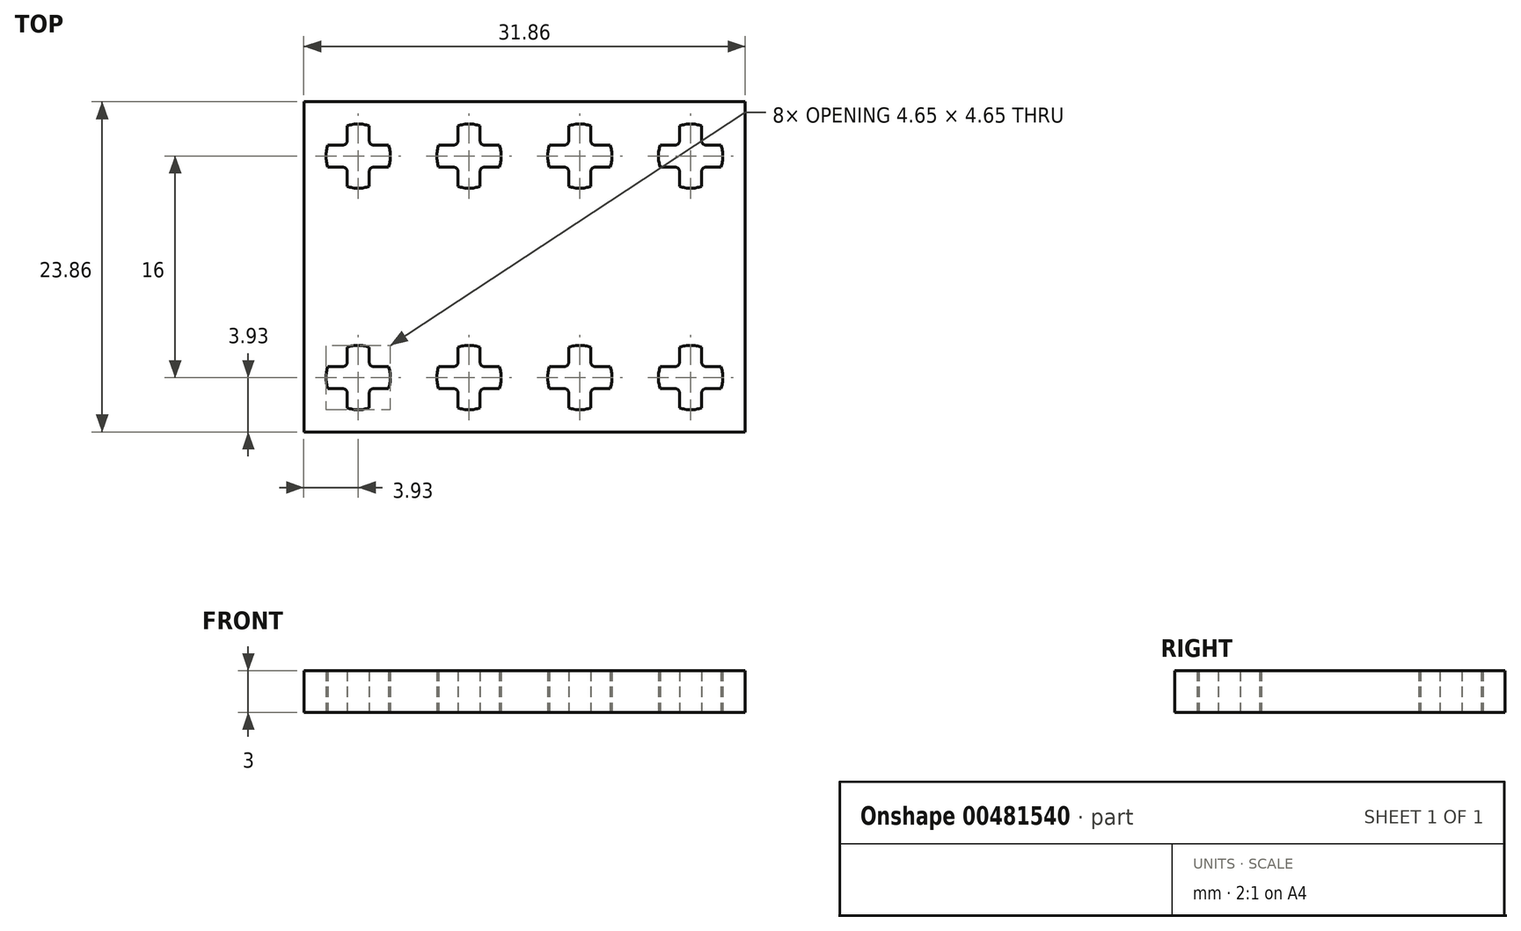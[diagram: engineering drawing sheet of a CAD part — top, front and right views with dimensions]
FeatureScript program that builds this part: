
annotation { "Feature Type Name" : "Feature", "Feature Type Description" : "" }
export const myFeature = defineFeature(function(context is Context, id is Id, definition is map)
    precondition{}
    {
        {
            var Q0;
            Q0=qCreatedBy(makeId("Top.planeOp"),FACE);
            var sketch = newSketch(context, id + "F0", { "sketchPlane" : qUnion([Q0])});
            skLineSegment(sketch, "E0.bottom", {"start": v(-16, 12) * mm, "end": v(16, 12) * mm, "construction": true});
            skLineSegment(sketch, "E0.top", {"start": v(-16, -12) * mm, "end": v(16, -12) * mm, "construction": true});
            skLineSegment(sketch, "E0.left", {"start": v(-16, 12) * mm, "end": v(-16, -12) * mm, "construction": true});
            skLineSegment(sketch, "E0.right", {"start": v(16, 12) * mm, "end": v(16, -12) * mm, "construction": true});
            skLineSegment(sketch, "E1", {"start": v(-12.8, 10.18) * mm, "end": v(-11.2, 10.18) * mm, "construction": true});
            skLineSegment(sketch, "E2", {"start": v(-11.2, 10.18) * mm, "end": v(-11.2, 9.1) * mm});
            skLineSegment(sketch, "E3", {"start": v(-10.9, 8.8) * mm, "end": v(-9.82, 8.8) * mm});
            skLineSegment(sketch, "E4", {"start": v(-9.82, 8.8) * mm, "end": v(-12, 8) * mm, "construction": true});
            skLineSegment(sketch, "E5", {"start": v(-12, 8) * mm, "end": v(-12.8, 10.18) * mm, "construction": true});
            skArc(sketch, "E6", {"start": v(-11.2, 10.18) * mm, "mid": v(-12, 10.33) * mm, "end": v(-12.8, 10.18) * mm});
            skArc(sketch, "E7", {"start": v(-11.2, 9.1) * mm, "mid": v(-11.11, 8.89) * mm, "end": v(-10.9, 8.8) * mm});
            skLineSegment(sketch, "E8", {"start": v(-11.2, 10.18) * mm, "end": v(-11.2, 8.8) * mm, "construction": true});
            skLineSegment(sketch, "E9", {"start": v(-11.2, 8.8) * mm, "end": v(-9.82, 8.8) * mm, "construction": true});
            skArc(sketch, "E10.1.0", {"start": v(-14.18, 8.8) * mm, "mid": v(-14.32, 8) * mm, "end": v(-14.18, 7.2) * mm});
            skArc(sketch, "E10.1.1", {"start": v(-13.1, 8.8) * mm, "mid": v(-12.89, 8.89) * mm, "end": v(-12.8, 9.1) * mm});
            skLineSegment(sketch, "E10.1.2", {"start": v(-14.18, 8.8) * mm, "end": v(-13.1, 8.8) * mm});
            skLineSegment(sketch, "E10.1.3", {"start": v(-12.8, 9.1) * mm, "end": v(-12.8, 10.18) * mm});
            skArc(sketch, "E10.2.0", {"start": v(-12.8, 5.82) * mm, "mid": v(-12, 5.67) * mm, "end": v(-11.2, 5.82) * mm});
            skArc(sketch, "E10.2.1", {"start": v(-12.8, 6.9) * mm, "mid": v(-12.89, 7.11) * mm, "end": v(-13.1, 7.2) * mm});
            skLineSegment(sketch, "E10.2.2", {"start": v(-12.8, 5.82) * mm, "end": v(-12.8, 6.9) * mm});
            skLineSegment(sketch, "E10.2.3", {"start": v(-13.1, 7.2) * mm, "end": v(-14.18, 7.2) * mm});
            skArc(sketch, "E10.3.0", {"start": v(-9.82, 7.2) * mm, "mid": v(-9.67, 8) * mm, "end": v(-9.82, 8.8) * mm});
            skArc(sketch, "E10.3.1", {"start": v(-10.9, 7.2) * mm, "mid": v(-11.11, 7.11) * mm, "end": v(-11.2, 6.9) * mm});
            skLineSegment(sketch, "E10.3.2", {"start": v(-9.82, 7.2) * mm, "end": v(-10.9, 7.2) * mm});
            skLineSegment(sketch, "E10.3.3", {"start": v(-11.2, 6.9) * mm, "end": v(-11.2, 5.82) * mm});
            skArc(sketch, "E11.1.0.0", {"start": v(-3.2, 10.18) * mm, "mid": v(-4, 10.32) * mm, "end": v(-4.8, 10.18) * mm});
            skArc(sketch, "E11.1.0.1", {"start": v(-2.9, 7.2) * mm, "mid": v(-3.11, 7.11) * mm, "end": v(-3.2, 6.9) * mm});
            skLineSegment(sketch, "E11.1.0.2", {"start": v(-1.82, 7.2) * mm, "end": v(-2.9, 7.2) * mm});
            skLineSegment(sketch, "E11.1.0.3", {"start": v(-5.1, 7.2) * mm, "end": v(-6.18, 7.2) * mm});
            skArc(sketch, "E11.1.0.4", {"start": v(-4.8, 6.9) * mm, "mid": v(-4.89, 7.11) * mm, "end": v(-5.1, 7.2) * mm});
            skLineSegment(sketch, "E11.1.0.5", {"start": v(-4.8, 9.1) * mm, "end": v(-4.8, 10.18) * mm});
            skLineSegment(sketch, "E11.1.0.6", {"start": v(-6.18, 8.8) * mm, "end": v(-5.1, 8.8) * mm});
            skArc(sketch, "E11.1.0.7", {"start": v(-5.1, 8.8) * mm, "mid": v(-4.89, 8.89) * mm, "end": v(-4.8, 9.1) * mm});
            skArc(sketch, "E11.1.0.8", {"start": v(-4.8, 5.82) * mm, "mid": v(-4, 5.67) * mm, "end": v(-3.2, 5.82) * mm});
            skArc(sketch, "E11.1.0.9", {"start": v(-6.18, 8.8) * mm, "mid": v(-6.32, 8) * mm, "end": v(-6.18, 7.2) * mm});
            skPoint(sketch, "E11.1.0.10", {"position": v(-4, 8) * mm});
            skLineSegment(sketch, "E11.1.0.11", {"start": v(-4.8, 5.82) * mm, "end": v(-4.8, 6.9) * mm});
            skArc(sketch, "E11.1.0.12", {"start": v(-1.82, 7.2) * mm, "mid": v(-1.67, 8) * mm, "end": v(-1.82, 8.8) * mm});
            skLineSegment(sketch, "E11.1.0.13", {"start": v(-3.2, 6.9) * mm, "end": v(-3.2, 5.82) * mm});
            skLineSegment(sketch, "E11.1.0.14", {"start": v(-3.2, 10.18) * mm, "end": v(-3.2, 9.1) * mm});
            skLineSegment(sketch, "E11.1.0.15", {"start": v(-2.9, 8.8) * mm, "end": v(-1.82, 8.8) * mm});
            skArc(sketch, "E11.1.0.16", {"start": v(-3.2, 9.1) * mm, "mid": v(-3.11, 8.89) * mm, "end": v(-2.9, 8.8) * mm});
            skArc(sketch, "E11.2.0.0", {"start": v(4.8, 10.18) * mm, "mid": v(4, 10.32) * mm, "end": v(3.2, 10.18) * mm});
            skArc(sketch, "E11.2.0.1", {"start": v(5.1, 7.2) * mm, "mid": v(4.89, 7.11) * mm, "end": v(4.8, 6.9) * mm});
            skLineSegment(sketch, "E11.2.0.2", {"start": v(6.18, 7.2) * mm, "end": v(5.1, 7.2) * mm});
            skLineSegment(sketch, "E11.2.0.3", {"start": v(2.9, 7.2) * mm, "end": v(1.82, 7.2) * mm});
            skArc(sketch, "E11.2.0.4", {"start": v(3.2, 6.9) * mm, "mid": v(3.11, 7.11) * mm, "end": v(2.9, 7.2) * mm});
            skLineSegment(sketch, "E11.2.0.5", {"start": v(3.2, 9.1) * mm, "end": v(3.2, 10.18) * mm});
            skLineSegment(sketch, "E11.2.0.6", {"start": v(1.82, 8.8) * mm, "end": v(2.9, 8.8) * mm});
            skArc(sketch, "E11.2.0.7", {"start": v(2.9, 8.8) * mm, "mid": v(3.11, 8.89) * mm, "end": v(3.2, 9.1) * mm});
            skArc(sketch, "E11.2.0.8", {"start": v(3.2, 5.82) * mm, "mid": v(4, 5.67) * mm, "end": v(4.8, 5.82) * mm});
            skArc(sketch, "E11.2.0.9", {"start": v(1.82, 8.8) * mm, "mid": v(1.68, 8) * mm, "end": v(1.82, 7.2) * mm});
            skPoint(sketch, "E11.2.0.10", {"position": v(4, 8) * mm});
            skLineSegment(sketch, "E11.2.0.11", {"start": v(3.2, 5.82) * mm, "end": v(3.2, 6.9) * mm});
            skArc(sketch, "E11.2.0.12", {"start": v(6.18, 7.2) * mm, "mid": v(6.33, 8) * mm, "end": v(6.18, 8.8) * mm});
            skLineSegment(sketch, "E11.2.0.13", {"start": v(4.8, 6.9) * mm, "end": v(4.8, 5.82) * mm});
            skLineSegment(sketch, "E11.2.0.14", {"start": v(4.8, 10.18) * mm, "end": v(4.8, 9.1) * mm});
            skLineSegment(sketch, "E11.2.0.15", {"start": v(5.1, 8.8) * mm, "end": v(6.18, 8.8) * mm});
            skArc(sketch, "E11.2.0.16", {"start": v(4.8, 9.1) * mm, "mid": v(4.89, 8.89) * mm, "end": v(5.1, 8.8) * mm});
            skLineSegment(sketch, "E11.direction1", {"start": v(-12.8, 5.82) * mm, "end": v(-4.8, 5.82) * mm, "construction": true});
            skLineSegment(sketch, "E11.direction2", {"start": v(-12.8, 5.82) * mm, "end": v(-12.8, -2.18) * mm, "construction": true});
            skLineSegment(sketch, "E12.bottom", {"start": v(-15.93, 11.93) * mm, "end": v(15.93, 11.92) * mm});
            skLineSegment(sketch, "E12.top", {"start": v(-15.93, -11.93) * mm, "end": v(15.92, -11.93) * mm});
            skLineSegment(sketch, "E12.left", {"start": v(-15.92, 11.92) * mm, "end": v(-15.92, -11.92) * mm});
            skLineSegment(sketch, "E12.right", {"start": v(15.93, 11.93) * mm, "end": v(15.93, -11.92) * mm});
            skArc(sketch, "E13.0.3.0", {"start": v(12.8, 10.18) * mm, "mid": v(12, 10.32) * mm, "end": v(11.2, 10.18) * mm});
            skArc(sketch, "E13.4.3.0", {"start": v(13.1, 7.2) * mm, "mid": v(12.89, 7.11) * mm, "end": v(12.8, 6.9) * mm});
            skLineSegment(sketch, "E13.8.3.0", {"start": v(14.18, 7.2) * mm, "end": v(13.1, 7.2) * mm});
            skLineSegment(sketch, "E13.11.3.0", {"start": v(10.9, 7.2) * mm, "end": v(9.82, 7.2) * mm});
            skArc(sketch, "E13.14.3.0", {"start": v(11.2, 6.9) * mm, "mid": v(11.11, 7.11) * mm, "end": v(10.9, 7.2) * mm});
            skLineSegment(sketch, "E13.18.3.0", {"start": v(11.2, 9.1) * mm, "end": v(11.2, 10.18) * mm});
            skLineSegment(sketch, "E13.21.3.0", {"start": v(9.82, 8.8) * mm, "end": v(10.9, 8.8) * mm});
            skArc(sketch, "E13.24.3.0", {"start": v(10.9, 8.8) * mm, "mid": v(11.11, 8.89) * mm, "end": v(11.2, 9.1) * mm});
            skArc(sketch, "E13.28.3.0", {"start": v(11.2, 5.82) * mm, "mid": v(12, 5.67) * mm, "end": v(12.8, 5.82) * mm});
            skArc(sketch, "E13.32.3.0", {"start": v(9.82, 8.8) * mm, "mid": v(9.68, 8) * mm, "end": v(9.82, 7.2) * mm});
            skPoint(sketch, "E13.36.3.0", {"position": v(12, 8) * mm});
            skLineSegment(sketch, "E13.37.3.0", {"start": v(11.2, 5.82) * mm, "end": v(11.2, 6.9) * mm});
            skArc(sketch, "E13.40.3.0", {"start": v(14.18, 7.2) * mm, "mid": v(14.33, 8) * mm, "end": v(14.18, 8.8) * mm});
            skLineSegment(sketch, "E13.44.3.0", {"start": v(12.8, 6.9) * mm, "end": v(12.8, 5.82) * mm});
            skLineSegment(sketch, "E13.47.3.0", {"start": v(12.8, 10.18) * mm, "end": v(12.8, 9.1) * mm});
            skLineSegment(sketch, "E13.50.3.0", {"start": v(13.1, 8.8) * mm, "end": v(14.18, 8.8) * mm});
            skArc(sketch, "E13.53.3.0", {"start": v(12.8, 9.1) * mm, "mid": v(12.89, 8.89) * mm, "end": v(13.1, 8.8) * mm});
            skLineSegment(sketch, "E14", {"start": v(-16, 8) * mm, "end": v(15.93, 8) * mm, "construction": true});
            skLineSegment(sketch, "E15", {"start": v(-12, 11.93) * mm, "end": v(-12, -12) * mm, "construction": true});
            skLineSegment(sketch, "E16.1.0.0", {"start": v(-16, 0) * mm, "end": v(15.93, 0) * mm, "construction": true});
            skLineSegment(sketch, "E16.2.0.0", {"start": v(-16, -8) * mm, "end": v(15.93, -8) * mm, "construction": true});
            skLineSegment(sketch, "E16.direction1", {"start": v(-16, 8) * mm, "end": v(-16, 0) * mm, "construction": true});
            skLineSegment(sketch, "E17.0.1.0", {"start": v(-4.1, 11.93) * mm, "end": v(-4.1, -12) * mm, "construction": true});
            skLineSegment(sketch, "E17.0.2.0", {"start": v(3.8, 11.93) * mm, "end": v(3.8, -12) * mm, "construction": true});
            skLineSegment(sketch, "E17.0.3.0", {"start": v(11.7, 11.93) * mm, "end": v(11.7, -12) * mm, "construction": true});
            skLineSegment(sketch, "E17.direction1", {"start": v(-35.3, -12) * mm, "end": v(-12, -12) * mm, "construction": true});
            skLineSegment(sketch, "E17.direction2", {"start": v(-12, -12) * mm, "end": v(-4.1, -12) * mm, "construction": true});
            skLineSegment(sketch, "E18.MirrorCS", {"start": v(-11.2, -10.18) * mm, "end": v(-11.2, -9.1) * mm});
            skArc(sketch, "E19.MirrorCS", {"start": v(-4.8, -6.9) * mm, "mid": v(-4.89, -7.11) * mm, "end": v(-5.1, -7.2) * mm});
            skArc(sketch, "E20.MirrorCS", {"start": v(13.1, -7.2) * mm, "mid": v(12.89, -7.11) * mm, "end": v(12.8, -6.9) * mm});
            skArc(sketch, "E21.MirrorCS", {"start": v(-2.9, -7.2) * mm, "mid": v(-3.11, -7.11) * mm, "end": v(-3.2, -6.9) * mm});
            skLineSegment(sketch, "E22.MirrorCS", {"start": v(-9.82, -8.8) * mm, "end": v(-12, -8) * mm, "construction": true});
            skArc(sketch, "E23.MirrorCS", {"start": v(-11.2, -9.1) * mm, "mid": v(-11.11, -8.89) * mm, "end": v(-10.9, -8.8) * mm});
            skLineSegment(sketch, "E24.MirrorCS", {"start": v(-10.9, -8.8) * mm, "end": v(-9.82, -8.8) * mm});
            skLineSegment(sketch, "E25.MirrorCS", {"start": v(-12.8, -10.18) * mm, "end": v(-11.2, -10.18) * mm, "construction": true});
            skArc(sketch, "E26.MirrorCS", {"start": v(-3.2, -9.1) * mm, "mid": v(-3.11, -8.89) * mm, "end": v(-2.9, -8.8) * mm});
            skArc(sketch, "E27.MirrorCS", {"start": v(-12.8, -6.9) * mm, "mid": v(-12.89, -7.11) * mm, "end": v(-13.1, -7.2) * mm});
            skLineSegment(sketch, "E28.MirrorCS", {"start": v(-12.8, -5.82) * mm, "end": v(-12.8, -6.9) * mm});
            skLineSegment(sketch, "E29.MirrorCS", {"start": v(-11.2, -8.8) * mm, "end": v(-9.82, -8.8) * mm, "construction": true});
            skArc(sketch, "E30.MirrorCS", {"start": v(-11.2, -10.18) * mm, "mid": v(-12, -10.33) * mm, "end": v(-12.8, -10.18) * mm});
            skLineSegment(sketch, "E31.MirrorCS", {"start": v(-11.2, -10.18) * mm, "end": v(-11.2, -8.8) * mm, "construction": true});
            skLineSegment(sketch, "E32.MirrorCS", {"start": v(4.8, -10.18) * mm, "end": v(4.8, -9.1) * mm});
            skArc(sketch, "E33.MirrorCS", {"start": v(12.8, -9.1) * mm, "mid": v(12.89, -8.89) * mm, "end": v(13.1, -8.8) * mm});
            skLineSegment(sketch, "E34.MirrorCS", {"start": v(-4.8, -5.82) * mm, "end": v(-4.8, -6.9) * mm});
            skArc(sketch, "E35.MirrorCS", {"start": v(-5.1, -8.8) * mm, "mid": v(-4.89, -8.89) * mm, "end": v(-4.8, -9.1) * mm});
            skArc(sketch, "E36.MirrorCS", {"start": v(11.2, -6.9) * mm, "mid": v(11.11, -7.11) * mm, "end": v(10.9, -7.2) * mm});
            skArc(sketch, "E37.MirrorCS", {"start": v(3.2, -6.9) * mm, "mid": v(3.11, -7.11) * mm, "end": v(2.9, -7.2) * mm});
            skArc(sketch, "E38.MirrorCS", {"start": v(5.1, -7.2) * mm, "mid": v(4.89, -7.11) * mm, "end": v(4.8, -6.9) * mm});
            skArc(sketch, "E39.MirrorCS", {"start": v(-10.9, -7.2) * mm, "mid": v(-11.11, -7.11) * mm, "end": v(-11.2, -6.9) * mm});
            skLineSegment(sketch, "E40.MirrorCS", {"start": v(-12.8, -9.1) * mm, "end": v(-12.8, -10.18) * mm});
            skLineSegment(sketch, "E41.MirrorCS", {"start": v(-12.8, -5.82) * mm, "end": v(-4.8, -5.82) * mm, "construction": true});
            skLineSegment(sketch, "E42.MirrorCS", {"start": v(-12, -8) * mm, "end": v(-12.8, -10.18) * mm, "construction": true});
            skArc(sketch, "E43.MirrorCS", {"start": v(4.8, -9.1) * mm, "mid": v(4.89, -8.89) * mm, "end": v(5.1, -8.8) * mm});
            skArc(sketch, "E44.MirrorCS", {"start": v(-13.1, -8.8) * mm, "mid": v(-12.89, -8.89) * mm, "end": v(-12.8, -9.1) * mm});
            skLineSegment(sketch, "E45.MirrorCS", {"start": v(12.8, -6.9) * mm, "end": v(12.8, -5.82) * mm});
            skLineSegment(sketch, "E46.MirrorCS", {"start": v(5.1, -8.8) * mm, "end": v(6.18, -8.8) * mm});
            skArc(sketch, "E47.MirrorCS", {"start": v(2.9, -8.8) * mm, "mid": v(3.11, -8.89) * mm, "end": v(3.2, -9.1) * mm});
            skArc(sketch, "E48.MirrorCS", {"start": v(-9.82, -7.2) * mm, "mid": v(-9.67, -8) * mm, "end": v(-9.82, -8.8) * mm});
            skLineSegment(sketch, "E49.MirrorCS", {"start": v(-13.1, -7.2) * mm, "end": v(-14.18, -7.2) * mm});
            skLineSegment(sketch, "E50.MirrorCS", {"start": v(2.9, -7.2) * mm, "end": v(1.82, -7.2) * mm});
            skLineSegment(sketch, "E51.MirrorCS", {"start": v(-11.2, -6.9) * mm, "end": v(-11.2, -5.82) * mm});
            skArc(sketch, "E52.MirrorCS", {"start": v(14.18, -7.2) * mm, "mid": v(14.33, -8) * mm, "end": v(14.18, -8.8) * mm});
            skLineSegment(sketch, "E53.MirrorCS", {"start": v(-3.2, -10.18) * mm, "end": v(-3.2, -9.1) * mm});
            skLineSegment(sketch, "E54.MirrorCS", {"start": v(-5.1, -7.2) * mm, "end": v(-6.18, -7.2) * mm});
            skArc(sketch, "E55.MirrorCS", {"start": v(10.9, -8.8) * mm, "mid": v(11.11, -8.89) * mm, "end": v(11.2, -9.1) * mm});
            skArc(sketch, "E56.MirrorCS", {"start": v(1.82, -8.8) * mm, "mid": v(1.68, -8) * mm, "end": v(1.82, -7.2) * mm});
            skLineSegment(sketch, "E57.MirrorCS", {"start": v(11.2, -9.1) * mm, "end": v(11.2, -10.18) * mm});
            skLineSegment(sketch, "E58.MirrorCS", {"start": v(10.9, -7.2) * mm, "end": v(9.82, -7.2) * mm});
            skLineSegment(sketch, "E59.MirrorCS", {"start": v(6.18, -7.2) * mm, "end": v(5.1, -7.2) * mm});
            skArc(sketch, "E60.MirrorCS", {"start": v(-3.2, -10.18) * mm, "mid": v(-4, -10.33) * mm, "end": v(-4.8, -10.18) * mm});
            skArc(sketch, "E61.MirrorCS", {"start": v(-1.82, -7.2) * mm, "mid": v(-1.67, -8) * mm, "end": v(-1.82, -8.8) * mm});
            skArc(sketch, "E62.MirrorCS", {"start": v(12.8, -10.18) * mm, "mid": v(12, -10.32) * mm, "end": v(11.2, -10.18) * mm});
            skLineSegment(sketch, "E63.MirrorCS", {"start": v(-3.2, -6.9) * mm, "end": v(-3.2, -5.82) * mm});
            skLineSegment(sketch, "E64.MirrorCS", {"start": v(3.2, -5.82) * mm, "end": v(3.2, -6.9) * mm});
            skLineSegment(sketch, "E65.MirrorCS", {"start": v(-6.18, -8.8) * mm, "end": v(-5.1, -8.8) * mm});
            skArc(sketch, "E66.MirrorCS", {"start": v(3.2, -5.82) * mm, "mid": v(4, -5.68) * mm, "end": v(4.8, -5.82) * mm});
            skLineSegment(sketch, "E67.MirrorCS", {"start": v(14.18, -7.2) * mm, "end": v(13.1, -7.2) * mm});
            skLineSegment(sketch, "E68.MirrorCS", {"start": v(13.1, -8.8) * mm, "end": v(14.18, -8.8) * mm});
            skArc(sketch, "E69.MirrorCS", {"start": v(-6.18, -8.8) * mm, "mid": v(-6.32, -8) * mm, "end": v(-6.18, -7.2) * mm});
            skLineSegment(sketch, "E70.MirrorCS", {"start": v(9.82, -8.8) * mm, "end": v(10.9, -8.8) * mm});
            skLineSegment(sketch, "E71.MirrorCS", {"start": v(-4.8, -9.1) * mm, "end": v(-4.8, -10.18) * mm});
            skArc(sketch, "E72.MirrorCS", {"start": v(9.82, -8.8) * mm, "mid": v(9.68, -8) * mm, "end": v(9.82, -7.2) * mm});
            skArc(sketch, "E73.MirrorCS", {"start": v(4.8, -10.18) * mm, "mid": v(4, -10.33) * mm, "end": v(3.2, -10.18) * mm});
            skArc(sketch, "E74.MirrorCS", {"start": v(-4.8, -5.82) * mm, "mid": v(-4, -5.68) * mm, "end": v(-3.2, -5.82) * mm});
            skLineSegment(sketch, "E75.MirrorCS", {"start": v(-1.82, -7.2) * mm, "end": v(-2.9, -7.2) * mm});
            skLineSegment(sketch, "E76.MirrorCS", {"start": v(3.2, -9.1) * mm, "end": v(3.2, -10.18) * mm});
            skLineSegment(sketch, "E77.MirrorCS", {"start": v(12.8, -10.18) * mm, "end": v(12.8, -9.1) * mm});
            skLineSegment(sketch, "E78.MirrorCS", {"start": v(4.8, -6.9) * mm, "end": v(4.8, -5.82) * mm});
            skLineSegment(sketch, "E79.MirrorCS", {"start": v(11.2, -5.82) * mm, "end": v(11.2, -6.9) * mm});
            skLineSegment(sketch, "E80.MirrorCS", {"start": v(-2.9, -8.8) * mm, "end": v(-1.82, -8.8) * mm});
            skArc(sketch, "E81.MirrorCS", {"start": v(11.2, -5.82) * mm, "mid": v(12, -5.67) * mm, "end": v(12.8, -5.82) * mm});
            skArc(sketch, "E82.MirrorCS", {"start": v(6.18, -7.2) * mm, "mid": v(6.33, -8) * mm, "end": v(6.18, -8.8) * mm});
            skLineSegment(sketch, "E83.MirrorCS", {"start": v(-9.82, -7.2) * mm, "end": v(-10.9, -7.2) * mm});
            skArc(sketch, "E84.MirrorCS", {"start": v(-14.18, -8.8) * mm, "mid": v(-14.32, -8) * mm, "end": v(-14.18, -7.2) * mm});
            skArc(sketch, "E85.MirrorCS", {"start": v(-12.8, -5.82) * mm, "mid": v(-12, -5.67) * mm, "end": v(-11.2, -5.82) * mm});
            skLineSegment(sketch, "E86.MirrorCS", {"start": v(-14.18, -8.8) * mm, "end": v(-13.1, -8.8) * mm});
            skLineSegment(sketch, "E87.MirrorCS", {"start": v(1.82, -8.8) * mm, "end": v(2.9, -8.8) * mm});
            skSolve(sketch);
        }
        {
            var Q0;
            Q0=makeQuery(id+"F0.imprint","IMPRINT",FACE,{"disambiguationData":[TD([[makeQuery(id+"F0.imprint","IMPRINT",EDGE,{"derivedFrom":sQuery(id+"F0.wireOp",EDGE,"E2")}),1.0]])]});
            extrude(context, id + "F1", {"entities" : qUnion([Q0]), "depth" : 3 * mm, "offsetDistance" : 25 * mm});
        }
    });
